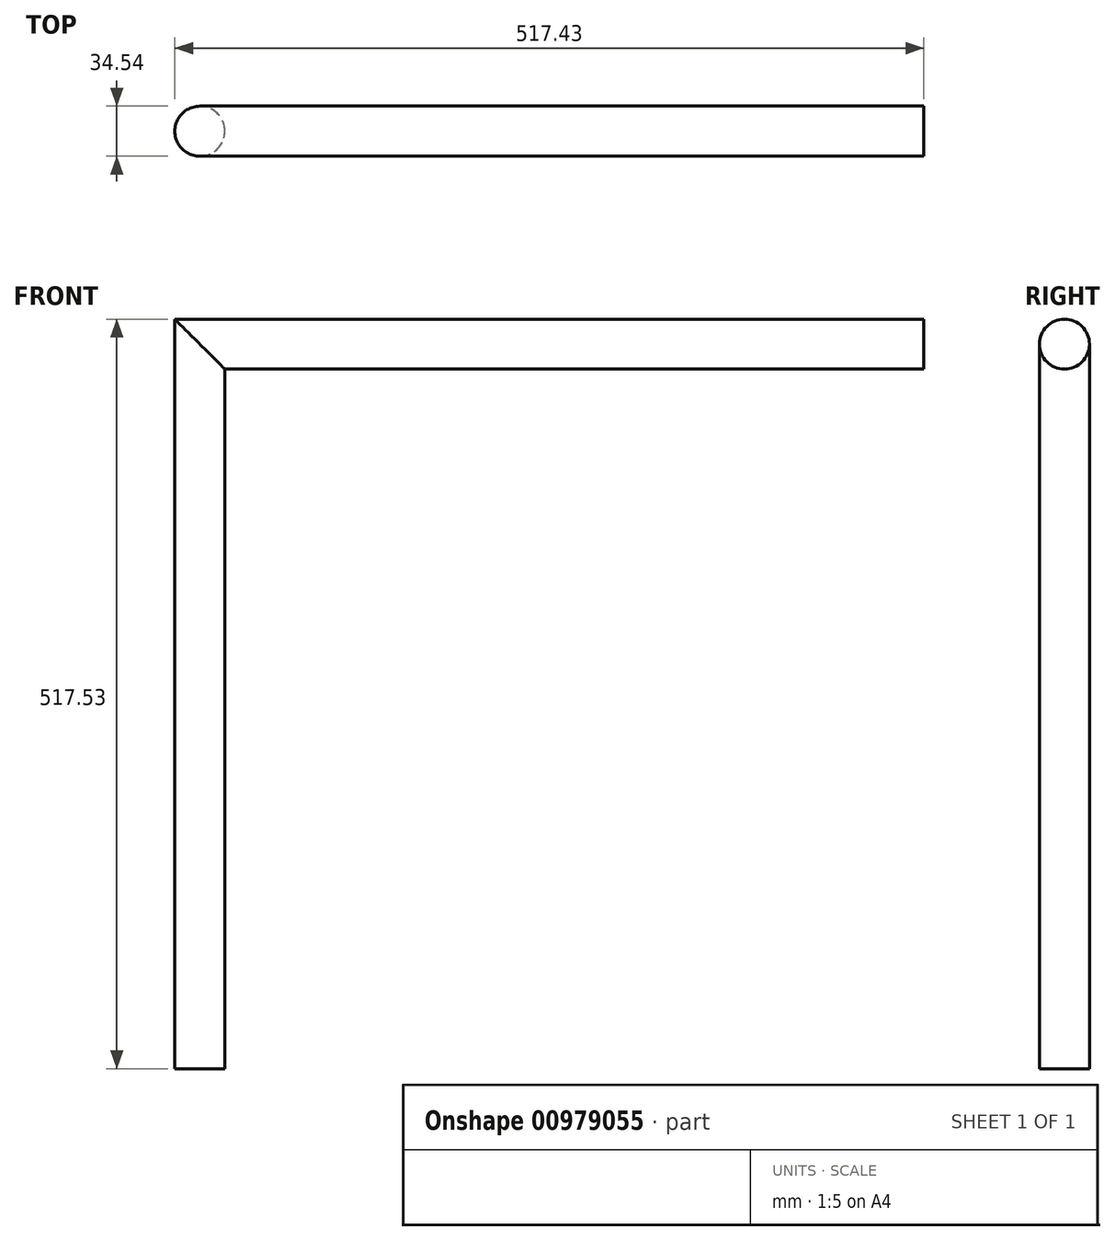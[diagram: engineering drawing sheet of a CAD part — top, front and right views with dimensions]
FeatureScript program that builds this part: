
annotation { "Feature Type Name" : "Feature", "Feature Type Description" : "" }
export const myFeature = defineFeature(function(context is Context, id is Id, definition is map)
    precondition{}
    {
        {
            var Q0;
            Q0=qCreatedBy(makeId("Top.planeOp"),FACE);
            var sketch = newSketch(context, id + "F0", { "sketchPlane" : qUnion([Q0])});
            skCircle(sketch, "E0", {"center": v(0, 0) * mm, "radius": 17.27 * mm});
            skSolve(sketch);
        }
        {
            var Q0;
            Q0=qCreatedBy(makeId("Front.planeOp"),FACE);
            var sketch = newSketch(context, id + "F1", { "sketchPlane" : qUnion([Q0])});
            skLineSegment(sketch, "E1", {"start": v(0, 0) * mm, "end": v(0, 500.25) * mm});
            skLineSegment(sketch, "E2", {"start": v(0, 500.25) * mm, "end": v(500.16, 500.25) * mm});
            skSolve(sketch);
        }
        {
            var Q0;
            Q0=qSketchRegion(id+"F0",true);
            var Q1;
            Q1=qConstructionFilter(qBodyType(qCreatedBy(id+"F1",EDGE),BodyType.WIRE),ConstructionObject.NO);
            sweep(context, id + "F2", {"profiles" : qUnion([Q0]), "path" : qUnion([Q1])});
        }
    });
